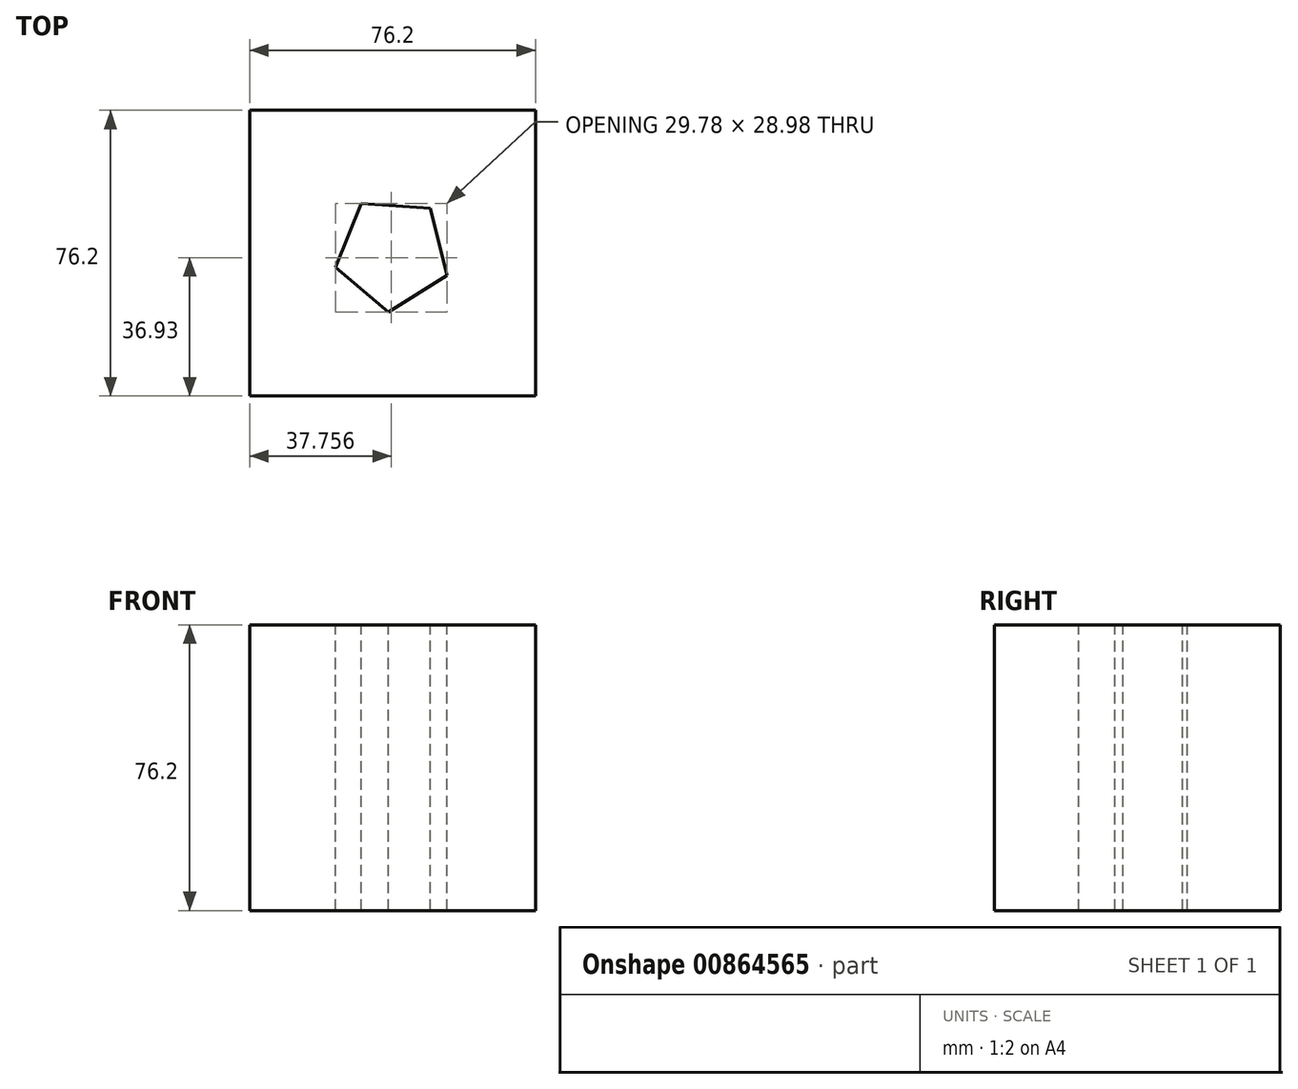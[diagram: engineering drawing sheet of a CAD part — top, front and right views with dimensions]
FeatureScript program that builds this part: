
annotation { "Feature Type Name" : "Feature", "Feature Type Description" : "" }
export const myFeature = defineFeature(function(context is Context, id is Id, definition is map)
    precondition{}
    {
        {
            var Q0;
            Q0=qCreatedBy(makeId("Top.planeOp"),FACE);
            var sketch = newSketch(context, id + "F0", { "sketchPlane" : qUnion([Q0])});
            skLineSegment(sketch, "E0.bottom", {"start": v(-45.21, 63.9) * mm, "end": v(30.99, 63.9) * mm});
            skLineSegment(sketch, "E0.top", {"start": v(-45.21, -12.3) * mm, "end": v(30.99, -12.3) * mm});
            skLineSegment(sketch, "E0.left", {"start": v(-45.21, 63.9) * mm, "end": v(-45.21, -12.3) * mm});
            skLineSegment(sketch, "E0.right", {"start": v(30.99, 63.9) * mm, "end": v(30.99, -12.3) * mm});
            skSolve(sketch);
        }
        {
            var Q0;
            Q0=makeQuery(id+"F0.imprint","IMPRINT",FACE,{"disambiguationData":[TD([[makeQuery(id+"F0.imprint","IMPRINT",EDGE,{"derivedFrom":sQuery(id+"F0.wireOp",EDGE,"E0.bottom")}),-1.0]])]});
            extrude(context, id + "F1", {"entities" : qUnion([Q0]), "depth" : 76.2 * mm, "offsetDistance" : 25.4 * mm});
        }
        {
            var Q0;
            Q0=makeQuery(id+"F1.opExtrude","CAP_FACE",FACE,{"disambiguationData":[OSD([sQuery(id+"F0.wireOp",EDGE,"E0.bottom"),sQuery(id+"F0.wireOp",EDGE,"E0.top"),sQuery(id+"F0.wireOp",EDGE,"E0.left"),sQuery(id+"F0.wireOp",EDGE,"E0.right")])],"isStart":false});
            var sketch = newSketch(context, id + "F2", { "sketchPlane" : qUnion([Q0])});
            skCircle(sketch, "E1.cCircle", {"center": v(-7.11, 25.8) * mm, "radius": 12.7 * mm, "construction": true});
            skLineSegment(sketch, "E1.0", {"start": v(7.44, 19.91) * mm, "end": v(-8.22, 10.15) * mm});
            skLineSegment(sketch, "E1.1", {"start": v(-8.22, 10.15) * mm, "end": v(-22.35, 22.03) * mm});
            skLineSegment(sketch, "E1.2", {"start": v(-22.35, 22.03) * mm, "end": v(-15.42, 39.13) * mm});
            skLineSegment(sketch, "E1.3", {"start": v(-15.42, 39.13) * mm, "end": v(3, 37.82) * mm});
            skLineSegment(sketch, "E1.4", {"start": v(3, 37.82) * mm, "end": v(7.44, 19.91) * mm});
            skPoint(sketch, "E1.0.midPoint", {"position": v(-0.4, 15.03) * mm});
            skSolve(sketch);
        }
        {
            var Q0;
            Q0=makeQuery(id+"F2.imprint","IMPRINT",FACE,{"disambiguationData":[TD([[makeQuery(id+"F2.imprint","IMPRINT",EDGE,{"derivedFrom":sQuery(id+"F2.wireOp",EDGE,"E1.0")}),-1.0]])]});
            var Q1;
            Q1 = qSketchRegion(id + "F2", true);
            extrude(context, id + "F3", {"entities" : qUnion([Q0, Q1]), "operationType" : NewBodyOperationType.REMOVE, "oppositeDirection" : true, "depth" : 76.2 * mm, "offsetDistance" : 25.4 * mm});
        }
    });
